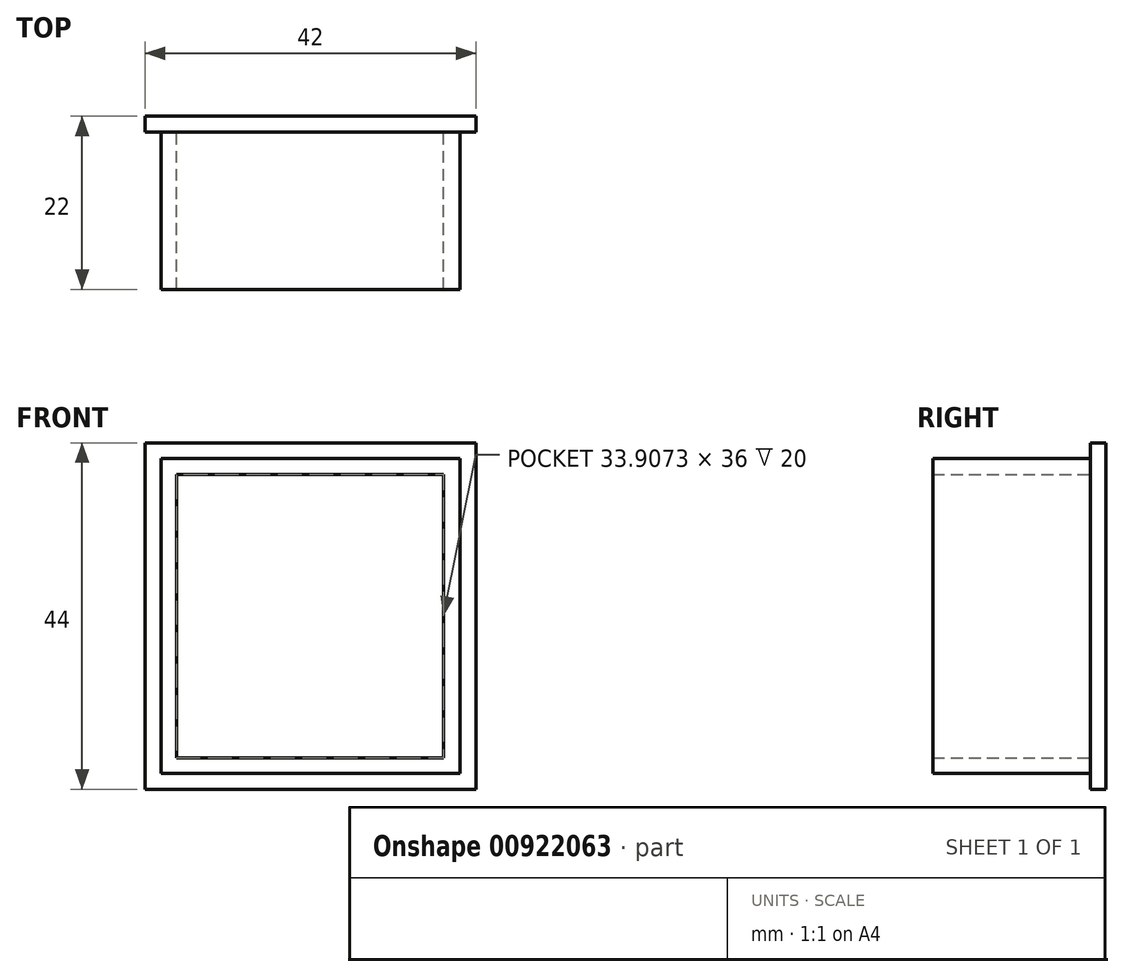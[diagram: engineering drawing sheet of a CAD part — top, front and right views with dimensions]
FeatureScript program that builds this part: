
annotation { "Feature Type Name" : "Feature", "Feature Type Description" : "" }
export const myFeature = defineFeature(function(context is Context, id is Id, definition is map)
    precondition{}
    {
        {
            var Q0;
            Q0=qCreatedBy(makeId("Front.planeOp"),FACE);
            var sketch = newSketch(context, id + "F0", { "sketchPlane" : qUnion([Q0])});
            skLineSegment(sketch, "E0.bottom", {"start": v(-17.96, -40.1) * mm, "end": v(20.04, -40.1) * mm});
            skLineSegment(sketch, "E0.top", {"start": v(-17.96, -0.1) * mm, "end": v(20.04, -0.1) * mm});
            skLineSegment(sketch, "E0.left", {"start": v(-17.96, -40.1) * mm, "end": v(-17.96, -0.1) * mm});
            skLineSegment(sketch, "E0.right", {"start": v(20.04, -40.1) * mm, "end": v(20.04, -0.1) * mm});
            skLineSegment(sketch, "E1.bottom", {"start": v(-15.96, -38.1) * mm, "end": v(17.95, -38.1) * mm});
            skLineSegment(sketch, "E1.top", {"start": v(-15.96, -2.1) * mm, "end": v(17.95, -2.1) * mm});
            skLineSegment(sketch, "E1.left", {"start": v(-15.96, -38.1) * mm, "end": v(-15.96, -2.1) * mm});
            skLineSegment(sketch, "E1.right", {"start": v(17.95, -38.1) * mm, "end": v(17.95, -2.1) * mm});
            skSolve(sketch);
        }
        {
            var Q0;
            Q0=makeQuery(id+"F0.imprint","IMPRINT",FACE,{"disambiguationData":[TD([[makeQuery(id+"F0.imprint","IMPRINT",EDGE,{"derivedFrom":sQuery(id+"F0.wireOp",EDGE,"E0.bottom")}),1.0]])]});
            extrude(context, id + "F1", {"entities" : qUnion([Q0]), "depth" : 20 * mm, "offsetDistance" : 25 * mm});
        }
        {
            var Q0;
            Q0=qCreatedBy(makeId("Front.planeOp"),FACE);
            var sketch = newSketch(context, id + "F2", { "sketchPlane" : qUnion([Q0])});
            skLineSegment(sketch, "E2.0", {"start": v(-19.96, -42.1) * mm, "end": v(-19.96, 1.9) * mm});
            skLineSegment(sketch, "E2.1", {"start": v(-19.96, -42.1) * mm, "end": v(22.04, -42.1) * mm});
            skLineSegment(sketch, "E2.2", {"start": v(22.04, -42.1) * mm, "end": v(22.04, 1.9) * mm});
            skLineSegment(sketch, "E2.3", {"start": v(-19.96, 1.9) * mm, "end": v(22.04, 1.9) * mm});
            skSolve(sketch);
        }
        {
            var Q0;
            Q0=makeQuery(id+"F2.imprint","IMPRINT",FACE,{"disambiguationData":[TD([[makeQuery(id+"F2.imprint","IMPRINT",EDGE,{"derivedFrom":sQuery(id+"F2.wireOp",EDGE,"E2.0")}),-1.0]])]});
            extrude(context, id + "F3", {"entities" : qUnion([Q0]), "operationType" : NewBodyOperationType.ADD, "oppositeDirection" : true, "depth" : 2 * mm, "offsetDistance" : 25 * mm});
        }
    });
